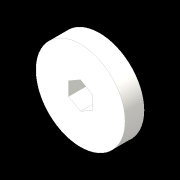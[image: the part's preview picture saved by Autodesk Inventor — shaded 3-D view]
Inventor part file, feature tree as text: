
AUTODESK INVENTOR PART (.ipt)
format: ipt  version: 2016 (Build 200138000, 138)  size: 81,408 bytes
history: native  units: in
note: dims shown in document units (in); Inventor stores cm internally (conversion verified against a paired STEP export)
features: extrude x1, sketch x1
ambient origin geometry x8: Origin, YZ Plane, XZ Plane, XY Plane, X Axis, Y Axis, Z Axis, Center Point
bodies: Solid1 (feature_tree)
feature tree (2):
  extrude  "Extrusion1"  Depth=0.5in
  sketch  "Sketch1"  dims[d0=1.875in d1=0.5in d2=0.4in d3=0.0in]
